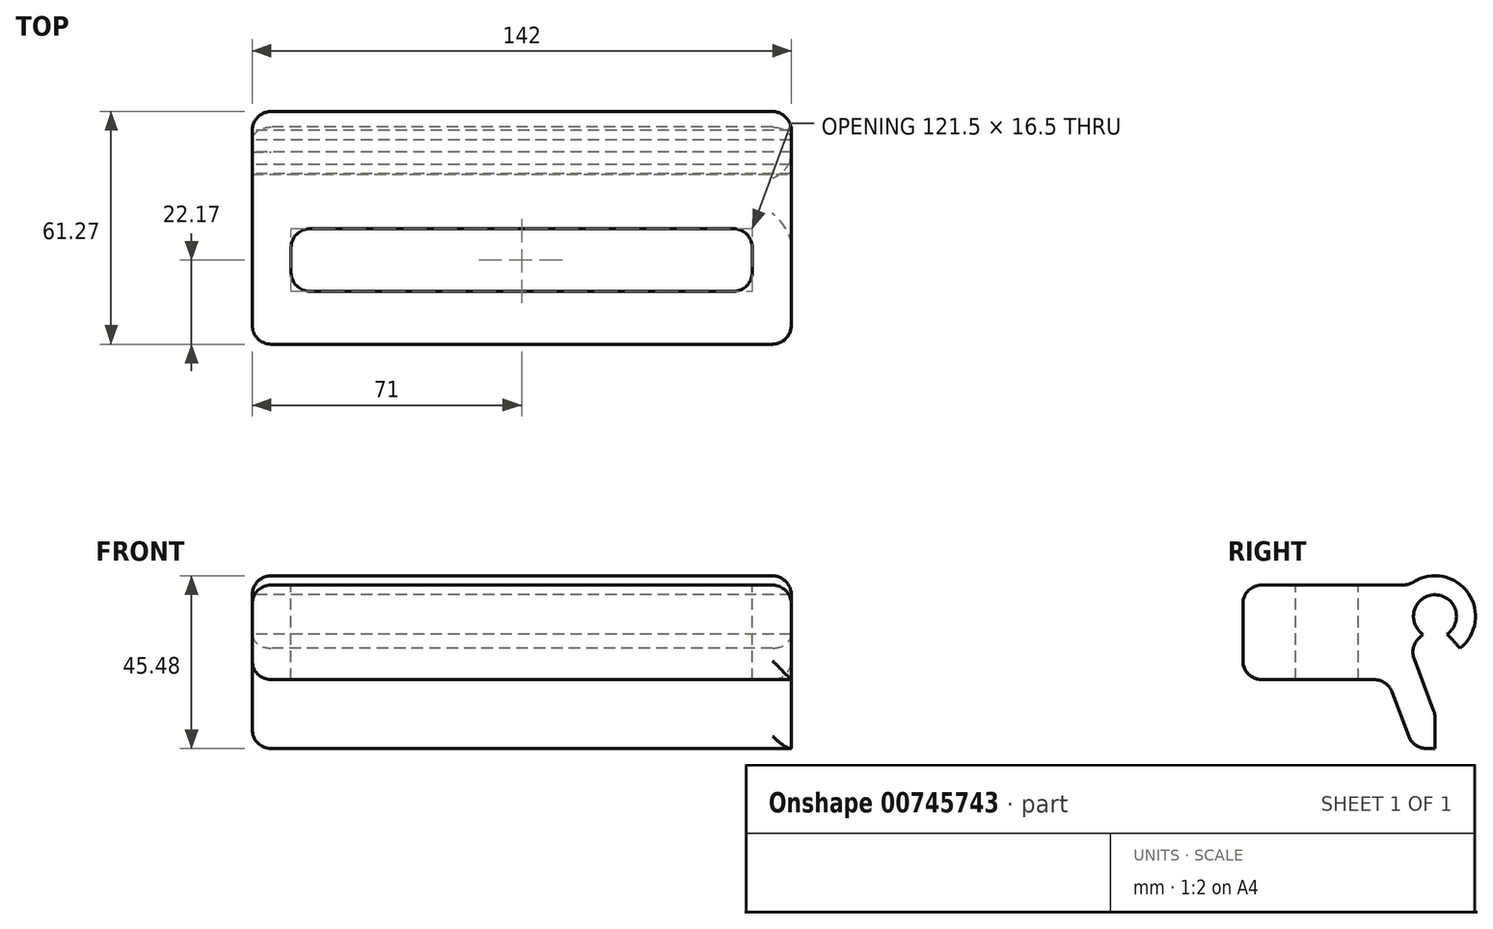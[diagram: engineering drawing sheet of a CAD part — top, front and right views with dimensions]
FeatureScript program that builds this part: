
annotation { "Feature Type Name" : "Feature", "Feature Type Description" : "" }
export const myFeature = defineFeature(function(context is Context, id is Id, definition is map)
    precondition{}
    {
        {
            var Q0;
            Q0=qCreatedBy(makeId("Right.planeOp"),FACE);
            var sketch = newSketch(context, id + "F0", { "sketchPlane" : qUnion([Q0])});
            skLineSegment(sketch, "E0", {"start": v(28.6, 0) * mm, "end": v(-22.17, 0) * mm});
            skLineSegment(sketch, "E1", {"start": v(-22.17, 0) * mm, "end": v(-22.17, -24.94) * mm});
            skLineSegment(sketch, "E2", {"start": v(-22.17, -24.94) * mm, "end": v(15.87, -24.94) * mm});
            skLineSegment(sketch, "E3", {"start": v(15.87, -24.94) * mm, "end": v(22.74, -43.06) * mm});
            skLineSegment(sketch, "E4", {"start": v(22.74, -43.06) * mm, "end": v(28.43, -43.06) * mm});
            skLineSegment(sketch, "E5", {"start": v(28.43, -43.06) * mm, "end": v(28.43, -24.94) * mm});
            skLineSegment(sketch, "E6", {"start": v(28.43, -24.94) * mm, "end": v(28.43, 0) * mm});
            skCircle(sketch, "E7", {"center": v(28.43, -8.25) * mm, "radius": 5.67 * mm});
            skCircle(sketch, "E8.0", {"center": v(28.43, -8.25) * mm, "radius": 10.67 * mm});
            skLineSegment(sketch, "E9", {"start": v(31.66, -12.9) * mm, "end": v(35, -16.65) * mm});
            skLineSegment(sketch, "E10", {"start": v(25.2, -12.9) * mm, "end": v(21.86, -16.65) * mm});
            skLineSegment(sketch, "E11", {"start": v(21.86, -16.65) * mm, "end": v(28.43, -34) * mm});
            skSolve(sketch);
        }
        {
            var Q0;
            {var subQ0=sQuery(id+"F0.wireOp",EDGE,"E1");Q0=makeQuery(id+"F0.imprint","IMPRINT",FACE,{"disambiguationData":[TD([[makeQuery(id+"F0.imprint","IMPRINT",EDGE,{"derivedFrom":subQ0}),1.0]])]});}
            var Q1;
            {var subQ0=sQuery(id+"F0.wireOp",EDGE,"E10");Q1=makeQuery(id+"F0.imprint","IMPRINT",FACE,{"disambiguationData":[TD([[makeQuery(id+"F0.imprint","IMPRINT",EDGE,{"derivedFrom":subQ0}),-1.0]])]});}
            var Q2;
            {var subQ0=sQuery(id+"F0.wireOp",EDGE,"E9");Q2=makeQuery(id+"F0.imprint","IMPRINT",FACE,{"disambiguationData":[TD([[makeQuery(id+"F0.imprint","IMPRINT",EDGE,{"derivedFrom":subQ0}),1.0]])]});}
            extrude(context, id + "F1", {"entities" : qUnion([Q0, Q1, Q2]), "depth" : 142 * mm, "offsetDistance" : 25 * mm});
        }
        {
            var Q0;
            Q0=makeQuery(id+"F1.opExtrude","SWEPT_EDGE",EDGE,{"disambiguationData":[OSD([sQuery(id+"F0.wireOp",EDGE,"E0"),sQuery(id+"F0.wireOp",EDGE,"E1")])]});
            var Q1;
            Q1=makeQuery(id+"F1.opExtrude","SWEPT_EDGE",EDGE,{"disambiguationData":[OSD([sQuery(id+"F0.wireOp",EDGE,"E1"),sQuery(id+"F0.wireOp",EDGE,"E2")])]});
            var Q2;
            Q2=makeQuery(id+"F1.opExtrude","CAP_EDGE",EDGE,{"disambiguationData":[OSD([sQuery(id+"F0.wireOp",EDGE,"E1")])],"isStart":false});
            var Q3;
            Q3=makeQuery(id+"F1.opExtrude","SWEPT_EDGE",EDGE,{"disambiguationData":[OSD([sQuery(id+"F0.wireOp",EDGE,"E8.0"),sQuery(id+"F0.wireOp",EDGE,"E10"),sQuery(id+"F0.wireOp",EDGE,"E11")])]});
            var Q4;
            Q4=makeQuery(id+"F1.opExtrude","SWEPT_EDGE",EDGE,{"disambiguationData":[OSD([sQuery(id+"F0.wireOp",EDGE,"E2"),sQuery(id+"F0.wireOp",EDGE,"E3")])]});
            var Q5;
            Q5=makeQuery(id+"F1.opExtrude","SWEPT_EDGE",EDGE,{"disambiguationData":[OSD([sQuery(id+"F0.wireOp",EDGE,"E5"),sQuery(id+"F0.wireOp",EDGE,"E11")])]});
            var Q6;
            Q6=makeQuery(id+"F1.opExtrude","SWEPT_EDGE",EDGE,{"disambiguationData":[OSD([sQuery(id+"F0.wireOp",EDGE,"E3"),sQuery(id+"F0.wireOp",EDGE,"E4")])]});
            var Q7;
            Q7=makeQuery(id+"F1.opExtrude","CAP_EDGE",EDGE,{"disambiguationData":[OSD([sQuery(id+"F0.wireOp",EDGE,"E3")])],"isStart":false});
            var Q8;
            Q8=makeQuery(id+"F1.opExtrude","CAP_EDGE",EDGE,{"disambiguationData":[OSD([sQuery(id+"F0.wireOp",EDGE,"E0")])],"isStart":false});
            var Q9;
            Q9=makeQuery(id+"F1.opExtrude","CAP_EDGE",EDGE,{"disambiguationData":[OSD([sQuery(id+"F0.wireOp",EDGE,"E8.0")])],"isStart":false});
            var Q10;
            Q10=makeQuery(id+"F1.opExtrude","CAP_EDGE",EDGE,{"disambiguationData":[OSD([sQuery(id+"F0.wireOp",EDGE,"E8.0")])],"isStart":true});
            var Q11;
            Q11=makeQuery(id+"F1.opExtrude","CAP_EDGE",EDGE,{"disambiguationData":[OSD([sQuery(id+"F0.wireOp",EDGE,"E0")])],"isStart":true});
            var Q12;
            Q12=makeQuery(id+"F1.opExtrude","SWEPT_EDGE",EDGE,{"disambiguationData":[OSD([sQuery(id+"F0.wireOp",EDGE,"E0"),sQuery(id+"F0.wireOp",EDGE,"E8.0")])]});
            fillet(context, id + "F2", {"entities" : qUnion([Q0, Q1, Q2, Q3, Q4, Q5, Q6, Q7, Q8, Q9, Q10, Q11, Q12]), "radius" : 5 * mm, "tangentPropagation" : true, "allowEdgeOverflow" : false});
        }
        {
            var Q0;
            Q0=makeQuery(id+"F1.opExtrude","SWEPT_FACE",FACE,{"disambiguationData":[OSD([sQuery(id+"F0.wireOp",EDGE,"E0")])]});
            var sketch = newSketch(context, id + "F3", { "sketchPlane" : qUnion([Q0])});
            skLineSegment(sketch, "E12.bottom", {"start": v(10.25, -8.25) * mm, "end": v(131.75, -8.25) * mm});
            skLineSegment(sketch, "E12.top", {"start": v(10.25, 8.25) * mm, "end": v(131.75, 8.25) * mm});
            skLineSegment(sketch, "E12.left", {"start": v(10.25, -8.25) * mm, "end": v(10.25, 8.25) * mm});
            skLineSegment(sketch, "E12.right", {"start": v(131.75, -8.25) * mm, "end": v(131.75, 8.25) * mm});
            skPoint(sketch, "E12.middle", {"position": v(71, 0) * mm});
            skSolve(sketch);
        }
        {
            var Q0;
            Q0=makeQuery(id+"F3.imprint","IMPRINT",FACE,{"disambiguationData":[TD([[makeQuery(id+"F3.imprint","IMPRINT",EDGE,{"derivedFrom":sQuery(id+"F3.wireOp",EDGE,"E12.bottom")}),1.0]])]});
            extrude(context, id + "F4", {"entities" : qUnion([Q0]), "operationType" : NewBodyOperationType.REMOVE, "endBound" : BoundingType.THROUGH_ALL, "oppositeDirection" : true, "depth" : 25 * mm, "offsetDistance" : 25 * mm});
        }
        {
            var Q0;
            Q0=makeQuery(id+"F4.boolean.opBoolean","COPY",EDGE,{"derivedFrom":makeQuery(id+"F4.opExtrude","SWEPT_EDGE",EDGE,{"disambiguationData":[OSD([sQuery(id+"F3.wireOp",EDGE,"E12.bottom"),sQuery(id+"F3.wireOp",EDGE,"E12.left")])]})});
            var Q1;
            Q1=makeQuery(id+"F4.boolean.opBoolean","COPY",EDGE,{"derivedFrom":makeQuery(id+"F4.opExtrude","SWEPT_EDGE",EDGE,{"disambiguationData":[OSD([sQuery(id+"F3.wireOp",EDGE,"E12.top"),sQuery(id+"F3.wireOp",EDGE,"E12.left")])]})});
            var Q2;
            Q2=makeQuery(id+"F4.boolean.opBoolean","COPY",EDGE,{"derivedFrom":makeQuery(id+"F4.opExtrude","SWEPT_EDGE",EDGE,{"disambiguationData":[OSD([sQuery(id+"F3.wireOp",EDGE,"E12.bottom"),sQuery(id+"F3.wireOp",EDGE,"E12.right")])]})});
            var Q3;
            Q3=makeQuery(id+"F4.boolean.opBoolean","COPY",EDGE,{"derivedFrom":makeQuery(id+"F4.opExtrude","SWEPT_EDGE",EDGE,{"disambiguationData":[OSD([sQuery(id+"F3.wireOp",EDGE,"E12.top"),sQuery(id+"F3.wireOp",EDGE,"E12.right")])]})});
            var Q4;
            Q4=makeQuery(id+"F4.boolean.opBoolean","COPY",EDGE,{"derivedFrom":makeQuery(id+"F4.opExtrude","CAP_EDGE",EDGE,{"disambiguationData":[OSD([sQuery(id+"F3.wireOp",EDGE,"E12.top")])],"isStart":true})});
            fillet(context, id + "F5", {"entities" : qUnion([Q0, Q1, Q2, Q3, Q4]), "radius" : 5 * mm, "tangentPropagation" : true, "allowEdgeOverflow" : false});
        }
        {
            var Q0;
            Q0=makeQuery(id+"F1.opExtrude","CAP_EDGE",EDGE,{"disambiguationData":[OSD([sQuery(id+"F0.wireOp",EDGE,"E1")])],"isStart":true});
            fillet(context, id + "F6", {"entities" : qUnion([Q0]), "radius" : 5 * mm, "tangentPropagation" : true, "allowEdgeOverflow" : false});
        }
    });
